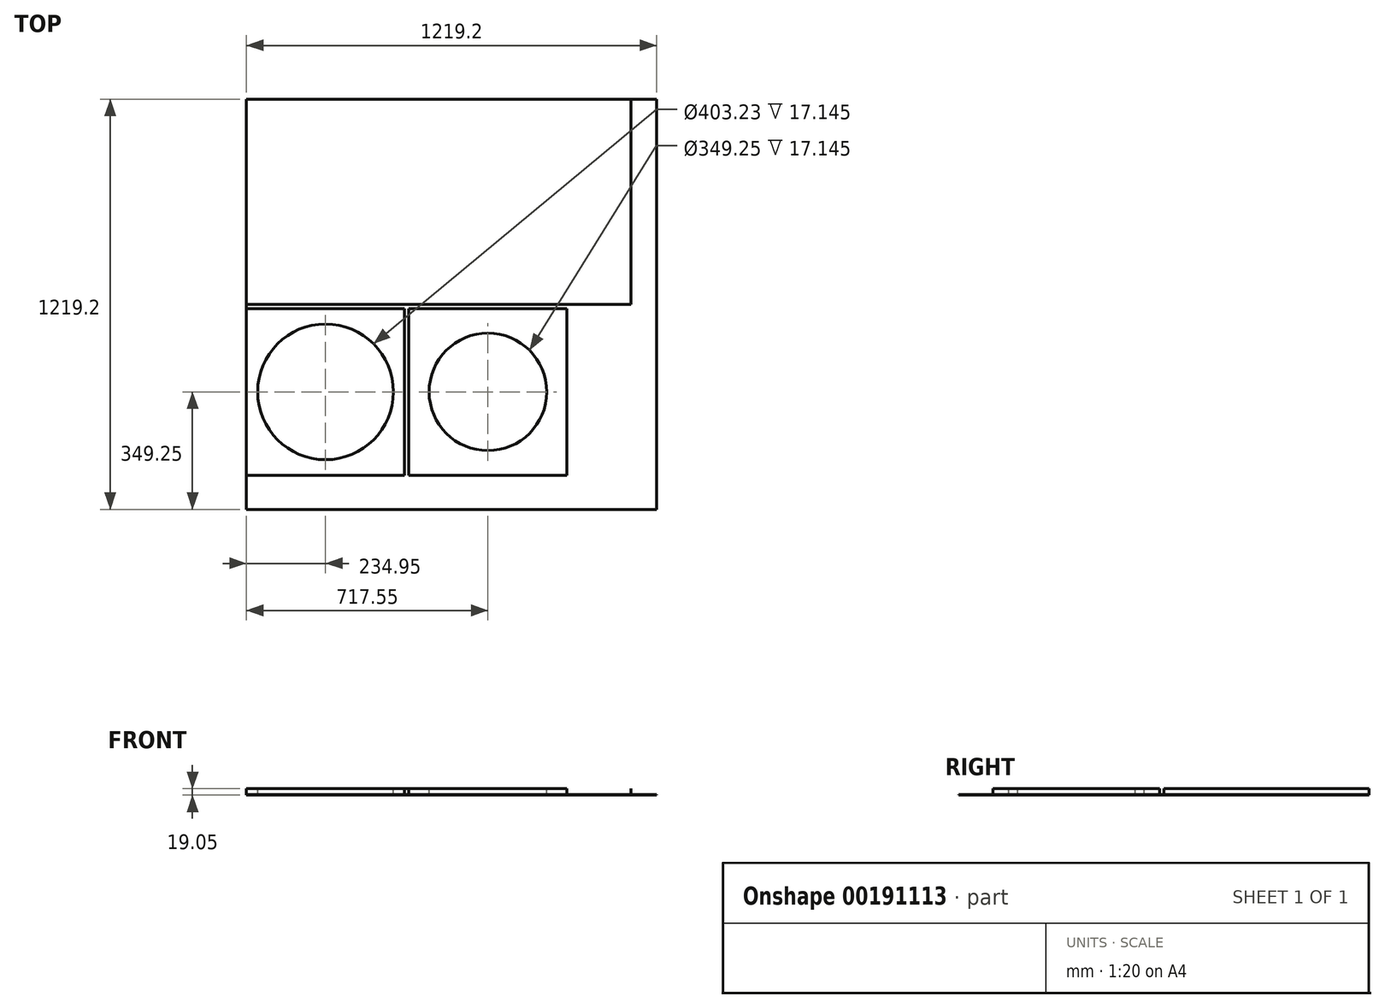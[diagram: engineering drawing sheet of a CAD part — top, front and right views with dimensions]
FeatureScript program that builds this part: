
annotation { "Feature Type Name" : "Feature", "Feature Type Description" : "" }
export const myFeature = defineFeature(function(context is Context, id is Id, definition is map)
    precondition{}
    {
        {
            var Q0;
            Q0=qCreatedBy(makeId("Top.planeOp"),FACE);
            var sketch = newSketch(context, id + "F0", { "sketchPlane" : qUnion([Q0])});
            skLineSegment(sketch, "E0.bottom", {"start": v(609.6, 609.6) * mm, "end": v(-609.6, 609.6) * mm});
            skLineSegment(sketch, "E0.top", {"start": v(609.6, -609.6) * mm, "end": v(-609.6, -609.6) * mm});
            skLineSegment(sketch, "E0.left", {"start": v(609.6, 609.6) * mm, "end": v(609.6, -609.6) * mm});
            skLineSegment(sketch, "E0.right", {"start": v(-609.6, 609.6) * mm, "end": v(-609.6, -609.6) * mm});
            skPoint(sketch, "E0.middle", {"position": v(0, 0) * mm});
            skSolve(sketch);
        }
        {
            var Q0;
            Q0 = qSketchRegion(id + "F0", true);
            extrude(context, id + "F1", {"entities" : qUnion([Q0]), "depth" : 19.05 * mm});
        }
        {
            var Q0;
            Q0=makeQuery(id+"F1.opExtrude","CAP_FACE",FACE,{"disambiguationData":[OSD([sQuery(id+"F0.wireOp",EDGE,"E0.bottom"),sQuery(id+"F0.wireOp",EDGE,"E0.top"),sQuery(id+"F0.wireOp",EDGE,"E0.left"),sQuery(id+"F0.wireOp",EDGE,"E0.right")])],"isStart":false});
            var sketch = newSketch(context, id + "F2", { "sketchPlane" : qUnion([Q0])});
            skLineSegment(sketch, "E1.bottom", {"start": v(-609.6, 609.6) * mm, "end": v(533.4, 609.6) * mm});
            skLineSegment(sketch, "E1.top", {"start": v(-609.6, 0) * mm, "end": v(533.4, 0) * mm});
            skLineSegment(sketch, "E1.left", {"start": v(-609.6, 609.6) * mm, "end": v(-609.6, 0) * mm});
            skLineSegment(sketch, "E1.right", {"start": v(533.4, 609.6) * mm, "end": v(533.4, 0) * mm});
            skLineSegment(sketch, "E2.bottom", {"start": v(-609.6, -12.7) * mm, "end": v(-139.7, -12.7) * mm});
            skLineSegment(sketch, "E2.top", {"start": v(-609.6, -508) * mm, "end": v(-139.7, -508) * mm});
            skLineSegment(sketch, "E2.left", {"start": v(-609.6, -12.7) * mm, "end": v(-609.6, -508) * mm});
            skLineSegment(sketch, "E2.right", {"start": v(-139.7, -12.7) * mm, "end": v(-139.7, -508) * mm});
            skLineSegment(sketch, "E3.bottom", {"start": v(-127, -12.7) * mm, "end": v(342.9, -12.7) * mm});
            skLineSegment(sketch, "E3.top", {"start": v(-127, -508) * mm, "end": v(342.9, -508) * mm});
            skLineSegment(sketch, "E3.left", {"start": v(-127, -12.7) * mm, "end": v(-127, -508) * mm});
            skLineSegment(sketch, "E3.right", {"start": v(342.9, -12.7) * mm, "end": v(342.9, -508) * mm});
            skCircle(sketch, "E4", {"center": v(-374.65, -260.35) * mm, "radius": 196.85 * mm, "construction": true});
            skCircle(sketch, "E5", {"center": v(107.95, -260.35) * mm, "radius": 176.21 * mm, "construction": true});
            skSolve(sketch);
        }
        {
            var Q0;
            {var subQ3=sQuery(id+"F2.wireOp",EDGE,"E1.top");Q0=makeQuery(id+"F2.imprint","IMPRINT",FACE,{"disambiguationData":[TD([[makeQuery(id+"F2.imprint","IMPRINT",EDGE,{"derivedFrom":subQ3}),-1.0]])]});}
            extrude(context, id + "F3", {"entities" : qUnion([Q0]), "operationType" : NewBodyOperationType.REMOVE, "oppositeDirection" : true, "depth" : 17.14 * mm});
        }
        {
            var Q0;
            {var subQ0=sQuery(id+"F0.wireOp",EDGE,"E0.right");Q0=makeQuery(id+"F3.boolean.opBoolean","SPLIT",FACE,{"disambiguationData":[TD([makeQuery(id+"F3.opExtrude","SWEPT_FACE",FACE,{"disambiguationData":[OSD([sQuery(id+"F2.wireOp",EDGE,"E2.bottom")])]})])],"derivedFrom":makeQuery(id+"F1.opExtrude","CAP_FACE",FACE,{"disambiguationData":[OSD([sQuery(id+"F0.wireOp",EDGE,"E0.bottom"),sQuery(id+"F0.wireOp",EDGE,"E0.top"),sQuery(id+"F0.wireOp",EDGE,"E0.left"),subQ0])],"isStart":false})});}
            var sketch = newSketch(context, id + "F4", { "sketchPlane" : qUnion([Q0])});
            skCircle(sketch, "E6", {"center": v(-374.65, -260.35) * mm, "radius": 201.61 * mm});
            skSolve(sketch);
        }
        {
            var Q0;
            Q0 = qSketchRegion(id + "F4", true);
            extrude(context, id + "F5", {"entities" : qUnion([Q0]), "operationType" : NewBodyOperationType.REMOVE, "oppositeDirection" : true, "depth" : 17.14 * mm});
        }
        {
            var Q0;
            Q0=makeQuery(id+"F3.boolean.opBoolean","SPLIT",FACE,{"disambiguationData":[TD([makeQuery(id+"F3.opExtrude","SWEPT_FACE",FACE,{"disambiguationData":[OSD([sQuery(id+"F2.wireOp",EDGE,"E3.bottom")])]})])],"derivedFrom":makeQuery(id+"F1.opExtrude","CAP_FACE",FACE,{"disambiguationData":[OSD([sQuery(id+"F0.wireOp",EDGE,"E0.bottom"),sQuery(id+"F0.wireOp",EDGE,"E0.top"),sQuery(id+"F0.wireOp",EDGE,"E0.left"),sQuery(id+"F0.wireOp",EDGE,"E0.right")])],"isStart":false})});
            var sketch = newSketch(context, id + "F6", { "sketchPlane" : qUnion([Q0])});
            skCircle(sketch, "E7", {"center": v(107.95, -260.35) * mm, "radius": 174.63 * mm});
            skSolve(sketch);
        }
        {
            var Q0;
            Q0 = qSketchRegion(id + "F6", true);
            extrude(context, id + "F7", {"entities" : qUnion([Q0]), "operationType" : NewBodyOperationType.REMOVE, "oppositeDirection" : true, "depth" : 17.14 * mm});
        }
    });
